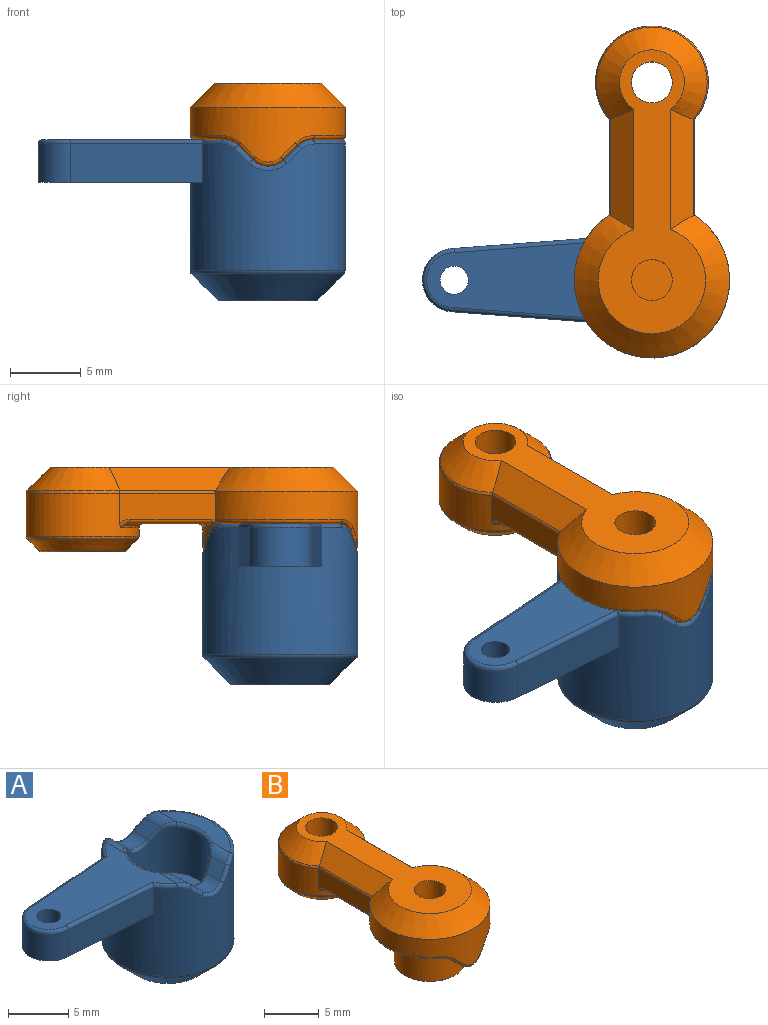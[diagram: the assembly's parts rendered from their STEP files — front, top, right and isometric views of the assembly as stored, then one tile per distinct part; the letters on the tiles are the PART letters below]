
ASSEMBLY  parts=2 mates=1
PART A: 53 faces, bbox 22.4x11.9x11.4 mm
  f0: torus R=5.2mm, axis (0,0,-1), area 8.1mm2, adj f1,f2
  f1: cylinder r=5.5mm len=11mm, axis (0,0,-1), area 281.4mm2, adj f0,f24,f25,f26,f27,f28,f29,f30
  f2: cone r=4.5mm half-angle=45deg, axis (0,0,1), area 75.7mm2, adj f0,f41
  f3: bspline ~1.21x1.04mm, area 0.5mm2, adj f4,f14,f20,f21
  f4: bspline ~2.34x0.81mm, area 1.1mm2, adj f3,f5,f21,f42
  f5: bspline ~1.21x1.04mm, area 0.5mm2, adj f4,f6,f21,f50
  f6: bspline ~1.09x1.07mm, area 0.5mm2, adj f5,f7,f21,f43
  f7: torus R=3.75mm, axis (0,0,-1), area 2mm2, adj f6,f8,f21,f40
  f8: bspline ~1.09x1.07mm, area 0.5mm2, adj f7,f9,f21,f39
  f9: bspline ~1.21x1.04mm, area 0.5mm2, adj f8,f10,f21,f38
  f10: bspline ~2.34x0.81mm, area 1.1mm2, adj f9,f11,f15,f21
  f11: bspline ~1.21x1.04mm, area 0.5mm2, adj f10,f12,f16,f21
  f12: bspline ~1.09x1.07mm, area 0.5mm2, adj f11,f13,f17,f21
  f13: torus R=3.75mm, axis (0,0,-1), area 2mm2, adj f12,f14,f18,f21
  f14: bspline ~1.09x1.07mm, area 0.5mm2, adj f3,f13,f19,f21
  f15: cylinder r=1.5mm len=2.12mm, axis (0,1,0), area 3.6mm2, adj f10,f16,f33,f38
  f16: plane 2.06x1mm, normal (-0.71,0,0.71), area 2.2mm2, adj f11,f15,f17,f32
  f17: cylinder r=1.5mm len=2.6mm, axis (0,1,0), area 2.2mm2, adj f12,f16,f18,f31
  f18: plane 8.32x2.08mm, normal (0,0,1), area 10.3mm2, adj f13,f17,f19,f30
  f19: cylinder r=1.5mm len=2.6mm, axis (0,1,0), area 2.2mm2, adj f14,f18,f20,f29
  f20: plane 2.06x1mm, normal (-0.71,0,0.71), area 2.2mm2, adj f3,f19,f28,f42
  f21: cylinder r=3.45mm len=6.9mm, axis (0,0,-1), area 91mm2, adj f3,f4,f5,f6,f7,f8,f9,f10
  f22: torus R=1.95mm, axis (0,0,1), area 3.2mm2, adj f23,f37,f40,f44
  f23: cylinder r=0.3mm len=9.56mm, axis (-1,-0.07,0), area 4.5mm2, adj f22,f36,f40,f45
  f24: torus R=5.2mm, axis (0,0,1), area 1mm2, adj f1,f25,f37,f40
  f25: bspline ~1.24x0.82mm, area 0.7mm2, adj f1,f24,f26,f43
  f26: bspline ~1.34x1.23mm, area 0.8mm2, adj f1,f25,f27,f50
  f27: bspline ~2.69x0.82mm, area 1.3mm2, adj f1,f26,f28,f42
  f28: bspline ~1.34x1.23mm, area 0.8mm2, adj f1,f20,f27,f29
  f29: bspline ~1.24x0.82mm, area 0.7mm2, adj f1,f19,f28,f30
  f30: torus R=5.2mm, axis (0,0,1), area 4.7mm2, adj f1,f18,f29,f31
  f31: bspline ~1.24x0.82mm, area 0.7mm2, adj f1,f17,f30,f32
  f32: bspline ~1.34x1.23mm, area 0.8mm2, adj f1,f16,f31,f33
  f33: bspline ~2.69x0.82mm, area 1.3mm2, adj f1,f15,f32,f34
  f34: bspline ~1.34x1.23mm, area 0.8mm2, adj f1,f33,f35,f38
  f35: bspline ~1.24x0.82mm, area 0.7mm2, adj f1,f34,f36,f39
  f36: torus R=5.2mm, axis (0,0,1), area 1mm2, adj f1,f23,f35,f40
  f37: cylinder r=0.3mm len=9.55mm, axis (1,-0.07,0), area 4.5mm2, adj f22,f24,f40,f46
  f38: plane 2.06x1mm, normal (0.71,0,0.71), area 2.2mm2, adj f9,f15,f34,f39
  f39: cylinder r=1.5mm len=2.6mm, axis (0,1,0), area 2.2mm2, adj f8,f35,f38,f40
  f40: plane 12.83x8.32mm, normal (0,0,1), area 54.5mm2, adj f7,f22,f23,f24,f36,f37,f39,f43
  f41: plane 7x7mm, normal (0,0,-1), area 31.9mm2, adj f2,f51
  f42: cylinder r=1.5mm len=2.12mm, axis (0,1,0), area 3.6mm2, adj f4,f20,f27,f50
  f43: cylinder r=1.5mm len=2.6mm, axis (0,1,0), area 2.2mm2, adj f6,f25,f40,f50
  f44: cylinder r=2.25mm len=4.5mm, axis (0,0,-1), area 19.1mm2, adj f22,f45,f46,f47
  f45: plane 9.37x2.7mm, normal (-0.07,1,0), area 25.4mm2, adj f1,f23,f44,f47
  f46: plane 9.36x2.7mm, normal (-0.07,-1,0), area 25.3mm2, adj f1,f37,f44,f47
  f47: plane 11.61x5.9mm, normal (0,0,-1), area 50.1mm2, adj f1,f44,f45,f46,f52
  f48: plane 2.9x2.9mm, normal (0,0,-1), area 6.6mm2, adj f51
  f49: plane 6.9x6.9mm, normal (0,0,1), area 37.4mm2, adj f21
  f50: plane 2.06x1mm, normal (0.71,0,0.71), area 2.2mm2, adj f5,f26,f42,f43
  f51: cylinder r=1.45mm len=5.4mm, axis (0,0,1), area 49.2mm2, adj f41,f48
  f52: cylinder r=1mm len=3mm, axis (0,0,1), area 18.8mm2, adj f40,f47
PART B: 60 faces, bbox 12.1x24x8.1 mm
  f0: bspline ~0.82x0.6mm, area 0.3mm2, adj f1,f3,f8,f9
  f1: cylinder r=0.3mm len=5.78mm, axis (0,-1,0), area 2.7mm2, adj f0,f2,f3,f15
  f2: bspline ~0.43x0.33mm, area 0.1mm2, adj f1,f3,f10,f25
  f3: plane 6.75x2.18mm, normal (1,0,0), area 12.7mm2, adj f0,f1,f2,f9,f17,f38
  f4: bspline ~0.43x0.33mm, area 0.1mm2, adj f5,f7,f12,f29
  f5: cylinder r=0.3mm len=5.78mm, axis (0,1,0), area 2.7mm2, adj f4,f6,f7,f15
  f6: bspline ~0.82x0.6mm, area 0.3mm2, adj f5,f7,f8,f9
  f7: plane 6.75x2.18mm, normal (-1,0,0), area 12.7mm2, adj f4,f5,f6,f9,f17,f39
  f8: torus R=4.3mm, axis (0,0,1), area 2.9mm2, adj f0,f6,f9,f15
  f9: cylinder r=4mm len=8mm, axis (0,0,-1), area 59.9mm2, adj f0,f3,f6,f7,f8,f46,f47
  f10: bspline ~0.92x0.88mm, area 0.3mm2, adj f2,f14,f15,f25
  f11: torus R=5.8mm, axis (0,0,1), area 1.8mm2, adj f13,f14,f15,f31
  f12: bspline ~0.92x0.88mm, area 0.3mm2, adj f4,f13,f15,f30
  f13: bspline ~0.33x0.3mm, area 0.1mm2, adj f11,f12,f15,f28
  f14: bspline ~0.33x0.3mm, area 0.1mm2, adj f10,f11,f15,f26
  f15: plane 5.78x5.4mm, normal (0,0,-1), area 24mm2, adj f1,f5,f8,f10,f11,f12,f13,f14
  f16: cone r=4.65mm half-angle=45deg, axis (0,0,-1), area 59.5mm2, adj f17,f38,f39,f40,f41,f42
  f17: cylinder r=5.5mm len=11mm, axis (0,0,1), area 62.3mm2, adj f3,f7,f16,f18,f19,f20,f21,f22
  f18: torus R=5.2mm, axis (0,0,1), area 4.7mm2, adj f17,f19,f29,f37
  f19: bspline ~1.35x0.98mm, area 0.6mm2, adj f17,f18,f20,f36
  f20: bspline ~1.21x1.18mm, area 0.6mm2, adj f17,f19,f21,f35
  f21: bspline ~2.13x0.71mm, area 1mm2, adj f17,f20,f22,f34
  f22: bspline ~1.21x1.18mm, area 0.6mm2, adj f17,f21,f23,f33
  f23: bspline ~1.35x0.98mm, area 0.6mm2, adj f17,f22,f24,f32
  f24: torus R=5.2mm, axis (0,0,1), area 4.7mm2, adj f17,f23,f25,f52
  f25: bspline ~1.35x0.98mm, area 0mm2, adj f2,f10,f17,f24,f26,f51
  f26: bspline ~1.21x1.18mm, area 0.6mm2, adj f14,f25,f27,f31,f53
  f27: bspline ~2.13x0.71mm, area 1mm2, adj f26,f28,f31,f49
  f28: bspline ~1.21x1.18mm, area 0.6mm2, adj f13,f27,f30,f31,f50
  f29: bspline ~1.35x0.98mm, area 0.2mm2, adj f4,f17,f18,f55
  f30: bspline ~1.35x0.98mm, area 0.2mm2, adj f12,f28,f55
  f31: cylinder r=5.5mm len=3.76mm, axis (0,0,1), area 2.6mm2, adj f11,f26,f27,f28
  f32: cylinder r=1.5mm len=3.96mm, axis (0,1,0), area 3.3mm2, adj f23,f33,f52,f54
  f33: plane 2.67x1.05mm, normal (0.71,0,-0.71), area 3.1mm2, adj f22,f32,f34,f54
  f34: cylinder r=1.5mm len=2.12mm, axis (0,1,0), area 4.8mm2, adj f21,f33,f35,f54
  f35: plane 2.67x1.05mm, normal (-0.71,0,-0.71), area 3.1mm2, adj f20,f34,f36,f54
  f36: cylinder r=1.5mm len=3.96mm, axis (0,1,0), area 3.3mm2, adj f19,f35,f37,f54
  f37: plane 8.32x2.08mm, normal (0,0,-1), area 11.9mm2, adj f18,f36,f54,f55
  f38: cylinder r=0.3mm len=6.83mm, axis (0,1,0), area 1.6mm2, adj f3,f16,f17,f42,f47
  f39: cylinder r=0.3mm len=6.83mm, axis (0,-1,0), area 1.6mm2, adj f7,f16,f17,f40,f47
  f40: plane 8.68x1.76mm, normal (-0.71,0,0.71), area 17.4mm2, adj f16,f39,f41,f48
  f41: plane 20.1x7.6mm, normal (0,0,1), area 69.8mm2, adj f16,f40,f42,f48,f58,f59
  f42: plane 8.68x1.76mm, normal (0.71,0,0.71), area 17.4mm2, adj f16,f38,f41,f48
  f43: torus R=2.88mm, axis (0,0,1), area 4.4mm2, adj f44,f45
  f44: cone r=3.5mm half-angle=45deg, axis (0,0,1), area 25.6mm2, adj f43,f46
  f45: plane 5.75x5.75mm, normal (0,0,-1), area 19.4mm2, adj f43,f59
  f46: torus R=3.7mm, axis (0,0,-1), area 5.9mm2, adj f9,f44
  f47: torus R=3.7mm, axis (0,0,1), area 4.3mm2, adj f9,f38,f39,f48
  f48: cone r=3.15mm half-angle=45deg, axis (0,0,-1), area 34.1mm2, adj f40,f41,f42,f47
  f49: cylinder r=1.5mm len=2.12mm, axis (0,1,0), area 4.8mm2, adj f27,f50,f53,f54
  f50: plane 2.67x1.05mm, normal (-0.71,0,-0.71), area 3.1mm2, adj f28,f49,f54,f55
  f51: cylinder r=1.5mm len=3.96mm, axis (0,1,0), area 3.3mm2, adj f25,f52,f53,f54
  f52: plane 8.32x2.08mm, normal (0,0,-1), area 11.9mm2, adj f24,f32,f51,f54
  f53: plane 2.67x1.05mm, normal (0.71,0,-0.71), area 3.1mm2, adj f26,f49,f51,f54
  f54: cylinder r=3.25mm len=6.5mm, axis (0,0,-1), area 69.4mm2, adj f32,f33,f34,f35,f36,f37,f49,f50
  f55: cylinder r=1.5mm len=3.96mm, axis (0,1,0), area 3.3mm2, adj f29,f30,f37,f50,f54
  f56: plane 2.9x2.9mm, normal (0,0,1), area 6.6mm2, adj f58
  f57: plane 6.5x6.5mm, normal (0,0,-1), area 33.2mm2, adj f54
  f58: cylinder r=1.45mm len=7mm, axis (0,0,1), area 63.8mm2, adj f41,f56
  f59: cylinder r=1.45mm len=6mm, axis (0,0,1), area 54.7mm2, adj f41,f45
PLACE A t=(0.19,0,0.35)mm
PLACE B t=(0.19,0,0.35)mm
MATE fastened A.f0 <-> B.f11  axis (0,0,1) through (0.19,0,3.35)mm
